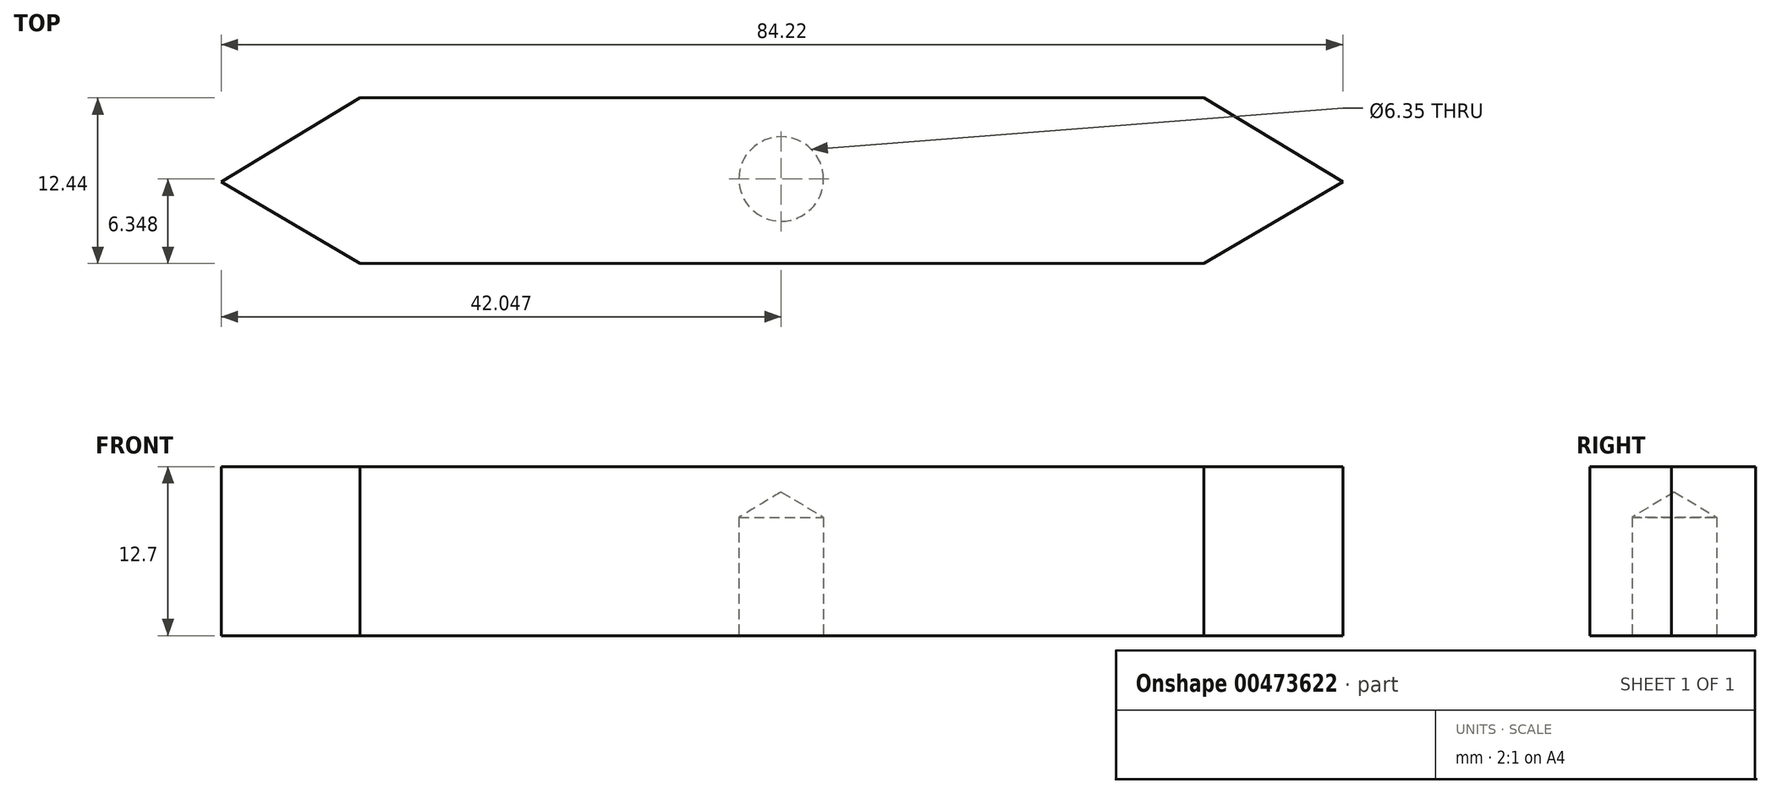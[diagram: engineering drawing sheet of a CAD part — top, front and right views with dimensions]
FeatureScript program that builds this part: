
annotation { "Feature Type Name" : "Feature", "Feature Type Description" : "" }
export const myFeature = defineFeature(function(context is Context, id is Id, definition is map)
    precondition{}
    {
        {
            var Q0;
            Q0=qCreatedBy(makeId("Top.planeOp"),FACE);
            var sketch = newSketch(context, id + "F0", { "sketchPlane" : qUnion([Q0])});
            skPoint(sketch, "E0.middle", {"position": v(0, 0) * mm});
            skLineSegment(sketch, "E1", {"start": v(0, 0) * mm, "end": v(10.42, 6.3) * mm});
            skLineSegment(sketch, "E2", {"start": v(10.42, 6.3) * mm, "end": v(73.8, 6.3) * mm});
            skLineSegment(sketch, "E3", {"start": v(73.8, 6.3) * mm, "end": v(84.22, 0) * mm});
            skLineSegment(sketch, "E4", {"start": v(84.22, 0) * mm, "end": v(73.8, -6.14) * mm});
            skLineSegment(sketch, "E5", {"start": v(73.8, -6.14) * mm, "end": v(10.42, -6.14) * mm});
            skLineSegment(sketch, "E6", {"start": v(10.42, -6.14) * mm, "end": v(0, 0) * mm});
            skLineSegment(sketch, "E7", {"start": v(-21.59, 0) * mm, "end": v(0, 0) * mm, "construction": true});
            skSolve(sketch);
        }
        {
            var Q0;
            Q0=makeQuery(id+"F0.imprint","IMPRINT",FACE,{"disambiguationData":[TD([[makeQuery(id+"F0.imprint","IMPRINT",EDGE,{"derivedFrom":sQuery(id+"F0.wireOp",EDGE,"E1")}),-1.0]])]});
            extrude(context, id + "F1", {"entities" : qUnion([Q0]), "depth" : 12.7 * mm});
        }
        {
            var Q0;
            Q0=makeQuery(id+"F1.opExtrude","CAP_FACE",FACE,{"disambiguationData":[OSD([sQuery(id+"F0.wireOp",EDGE,"E1"),sQuery(id+"F0.wireOp",EDGE,"E2"),sQuery(id+"F0.wireOp",EDGE,"E3"),sQuery(id+"F0.wireOp",EDGE,"E4"),sQuery(id+"F0.wireOp",EDGE,"E5"),sQuery(id+"F0.wireOp",EDGE,"E6")])],"isStart":true});
            var sketch = newSketch(context, id + "F2", { "sketchPlane" : qUnion([Q0])});
            skPoint(sketch, "E8", {"position": v(42.05, -0.2) * mm});
            skSolve(sketch);
        }
        {
            var Q0;
            Q0=sQuery(id+"F2.wireOp",VERTEX,"E8");
            var Q1;
            Q1=makeQuery(id+"F1.opExtrude","SWEPT_BODY",BODY,{"disambiguationData":[OSD([sQuery(id+"F0.wireOp",EDGE,"E1"),sQuery(id+"F0.wireOp",EDGE,"E2"),sQuery(id+"F0.wireOp",EDGE,"E3"),sQuery(id+"F0.wireOp",EDGE,"E4"),sQuery(id+"F0.wireOp",EDGE,"E5"),sQuery(id+"F0.wireOp",EDGE,"E6")])]});
            hole(context, id + "F3", {"style" : HoleStyle.SIMPLE, "endStyle" : HoleEndStyle.BLIND, "holeDiameter" : 6.35 * mm, "holeDepth" : 8.9 * mm, "isTappedThrough" : true, "tappedDepth" : 12.7 * mm, "tapClearance" : 3, "locations" : qUnion([Q0]), "scope" : qUnion([Q1])});
        }
    });
